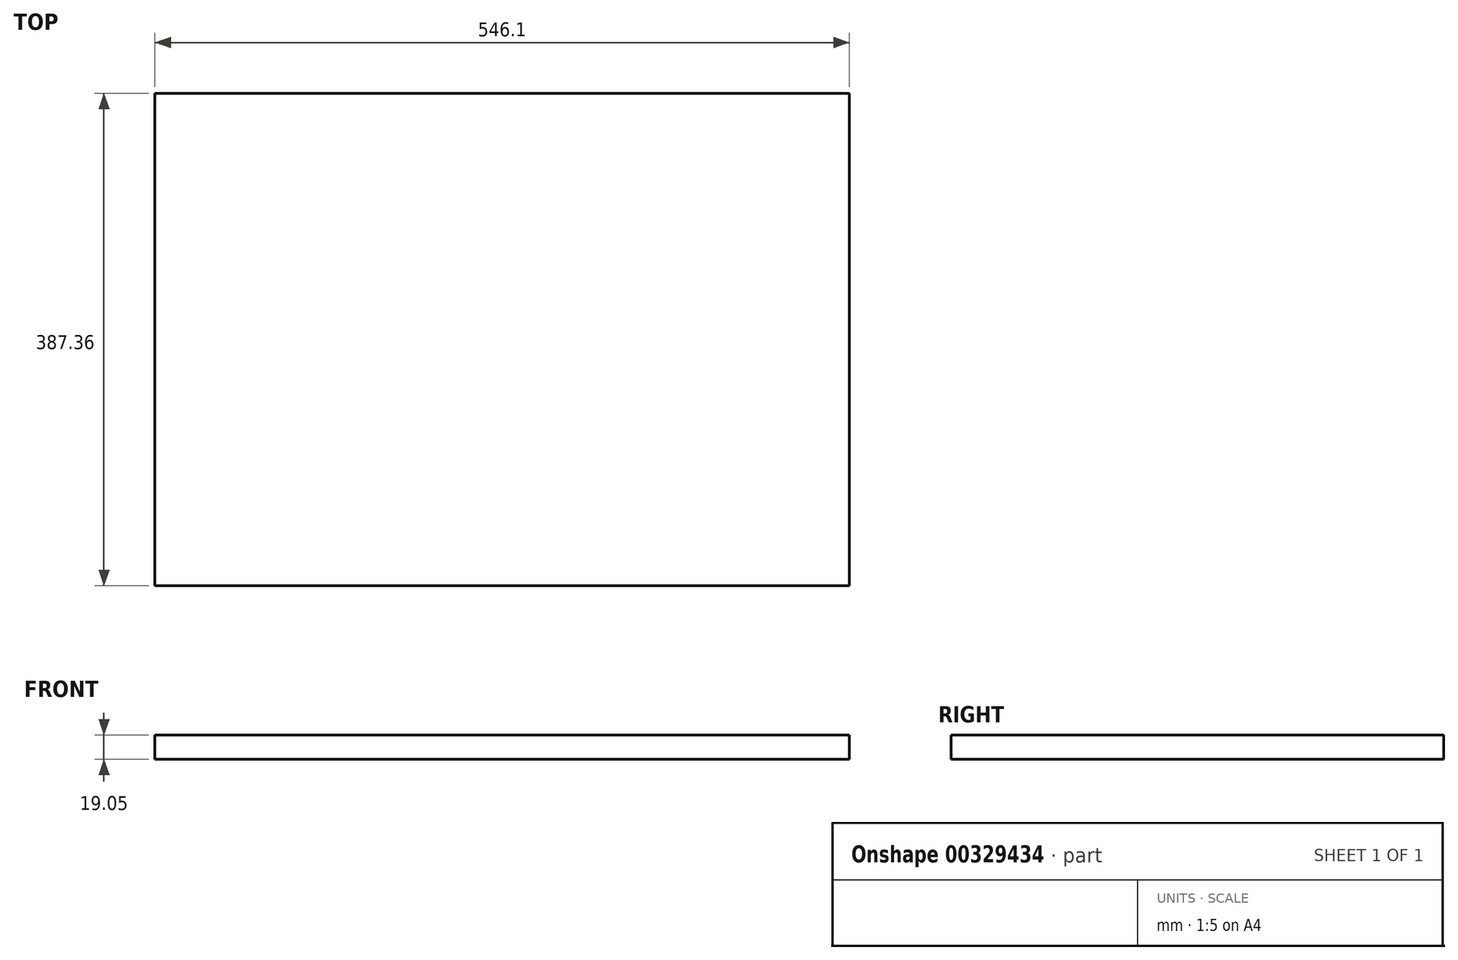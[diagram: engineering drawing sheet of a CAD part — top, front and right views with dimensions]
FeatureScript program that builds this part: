
annotation { "Feature Type Name" : "Feature", "Feature Type Description" : "" }
export const myFeature = defineFeature(function(context is Context, id is Id, definition is map)
    precondition{}
    {
        {
            var Q0;
            Q0=qCreatedBy(makeId("Top.planeOp"),FACE);
            var sketch = newSketch(context, id + "F0", { "sketchPlane" : qUnion([Q0])});
            skLineSegment(sketch, "E0.bottom", {"start": v(273.05, 193.68) * mm, "end": v(-273.05, 193.67) * mm});
            skLineSegment(sketch, "E0.top", {"start": v(273.05, -193.67) * mm, "end": v(-273.05, -193.68) * mm});
            skLineSegment(sketch, "E0.left", {"start": v(273.05, 193.68) * mm, "end": v(273.05, -193.67) * mm});
            skLineSegment(sketch, "E0.right", {"start": v(-273.05, 193.67) * mm, "end": v(-273.05, -193.68) * mm});
            skPoint(sketch, "E0.middle", {"position": v(0, 0) * mm});
            skSolve(sketch);
        }
        {
            var Q0;
            Q0=qSketchRegion(id+"F0",true);
            extrude(context, id + "F1", {"entities" : qUnion([Q0]), "depth" : 19.05 * mm});
        }
    });
